# Revit family: MR_ОсветительныйПрибор_Ego_Боллард
name_source: partatom
category: Осветительные приборы
units: mm (PartAtom-declared; Revit-internal decimal feet)

## family parameters
Всегда вертикально = Да
Источник света = Да
На основе рабочей плоскости = Да
Общий = Да
При загрузке вырезать с полостями = Нет
Размер круглого соединителя = Использовать диаметр
Тип детали = Нормальный
Точка расчета площади = Нет

## types (4) — shared parameters
ADSK_URL страницы изделия = https://martinirus.ru
ADSK_Группирование = Наружное освещение_светильник
ADSK_Единица измерения = шт.
ADSK_Завод-изготовитель = MartiniRUS
ADSK_Классификация нагрузок = Освещение
ADSK_Количество = 1
ADSK_Количество фаз = 1
ADSK_Количество фаз числовое = 1
ADSK_Коэффициент мощности = 0.98
ADSK_Материал = <По категории>
ADSK_Напряжение = 230 В
ADSK_Номинальная мощность = 13 Вт
ADSK_Полная мощность = 13 В·А
ADSK_Ток = 0 А
IP Class = IP65
Видимая форма излучения при визуализации = Да
Группа модели = Ego
Закладной элемент тип 5 370х370х400 = Нет
Излучение по диаметру окружности = 30 мм
Класс Защиты = I
Климатическая зона = УХЛ1
Описание = Ego боллард
Отметка по умолчанию = 1219 мм
Полная установленная мощность = 13 В·А
Самосветящий материал = Источник света по умолчанию
Светофильтр = 16777215
Смещение цветовой температуры при затухании лампы = <Нет>
Угол наклона = 90.00°

## per-type parameters (varying)
| type | ADSK_Код изделия | ADSK_Масса | ADSK_Размер_Высота | Боллард_1900mm | Закладной элемент тип 1 L_1500мм | Закладной элемент тип 1 L_500мм | НижнийБлок | Файл фотометрической сетки |
| Ego_Боллард_1900mm_3000k | P864674__WW | 20 | 1900 мм | Да | Да | Нет | 380 мм | P864674NCWW.ies |
| Ego_Боллард_1900mm_4000k | P864674__NW | 20 | 1900 мм | Да | Да | Нет | 380 мм | P864674NCNW.ies |
| Ego_Боллард_800mm_4000k | P864687__NW | 10 | 800 мм | Нет | Нет | Да | 160 мм | P864687NCNW.ies |
| Ego_Боллард_800mm_3000k | P864687__WW | 10 | 800 мм | Нет | Нет | Да | 160 мм | P864687NCWW.ies |

note: column(s) folded — value = type name in every type: ADSK_Наименование

## geometry (parser evidence)
native form markers: Blend x8
no freeform markers — native parametric forms only
